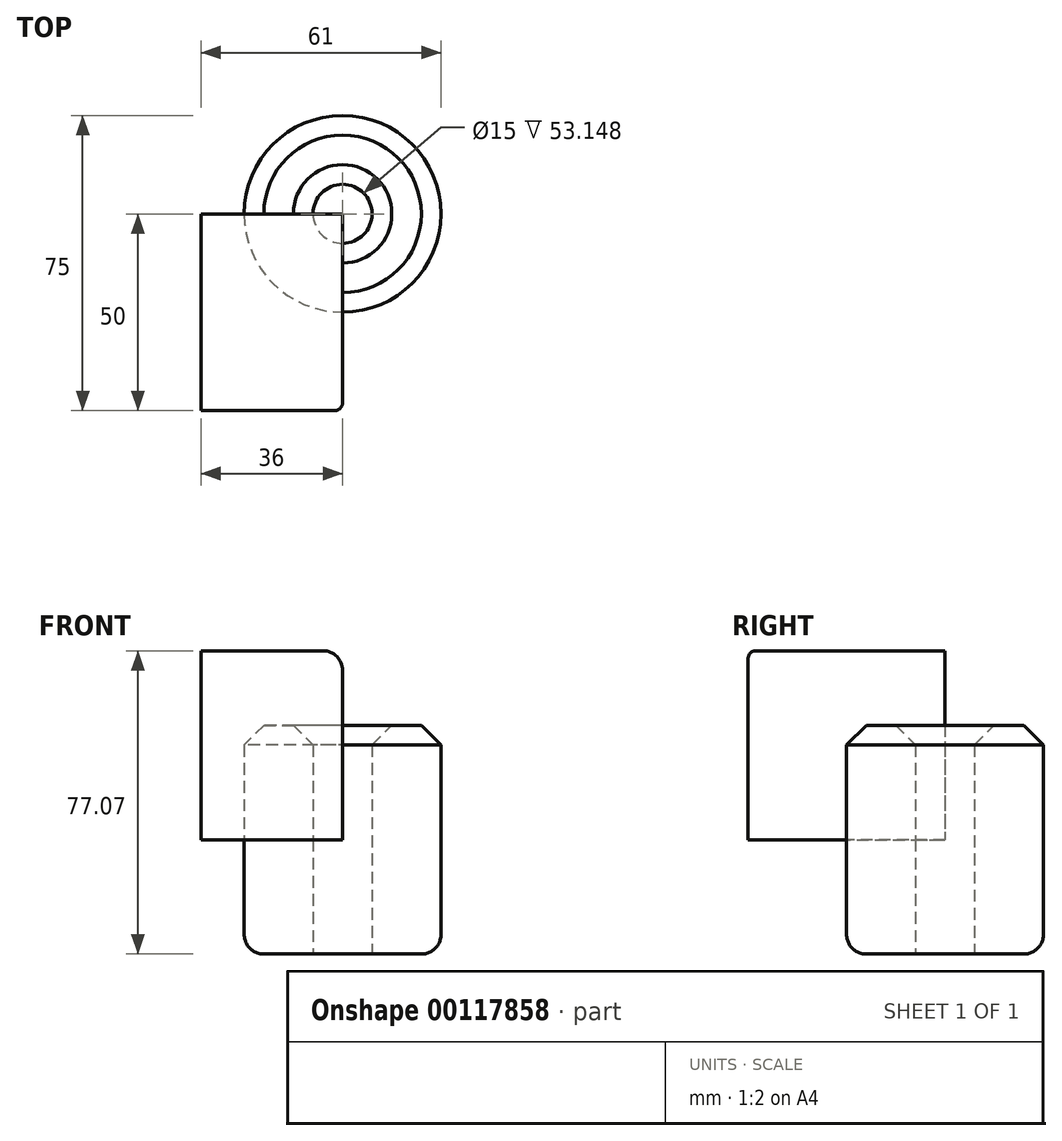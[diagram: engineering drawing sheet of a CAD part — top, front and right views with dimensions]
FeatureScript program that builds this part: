
annotation { "Feature Type Name" : "Feature", "Feature Type Description" : "" }
export const myFeature = defineFeature(function(context is Context, id is Id, definition is map)
    precondition{}
    {
        {
            var Q0;
            Q0=qCreatedBy(makeId("Top.planeOp"),FACE);
            var sketch = newSketch(context, id + "F0", { "sketchPlane" : qUnion([Q0])});
            skCircle(sketch, "E0", {"center": v(0, 0) * mm, "radius": 7.5 * mm});
            skCircle(sketch, "E1", {"center": v(0, 0) * mm, "radius": 25 * mm});
            skSolve(sketch);
        }
        {
            var Q0;
            Q0=makeQuery(id+"F0.imprint","IMPRINT",FACE,{"disambiguationData":[TD([[makeQuery(id+"F0.imprint","IMPRINT",EDGE,{"derivedFrom":sQuery(id+"F0.wireOp",EDGE,"E0")}),-1.0]])]});
            extrude(context, id + "F1", {"entities" : qUnion([Q0]), "endBound" : BoundingType.SYMMETRIC, "depth" : 58.15 * mm});
        }
        {
            var Q0;
            Q0=qCreatedBy(makeId("Front.planeOp"),FACE);
            var sketch = newSketch(context, id + "F2", { "sketchPlane" : qUnion([Q0])});
            skLineSegment(sketch, "E2.bottom", {"start": v(-36, 48) * mm, "end": v(0, 48) * mm});
            skLineSegment(sketch, "E2.top", {"start": v(-36, 0) * mm, "end": v(0, 0) * mm});
            skLineSegment(sketch, "E2.left", {"start": v(-36, 48) * mm, "end": v(-36, 0) * mm});
            skLineSegment(sketch, "E2.right", {"start": v(0, 48) * mm, "end": v(0, 0) * mm});
            skSolve(sketch);
        }
        {
            var Q0;
            Q0=makeQuery(id+"F2.imprint","IMPRINT",FACE,{"disambiguationData":[TD([[makeQuery(id+"F2.imprint","IMPRINT",EDGE,{"derivedFrom":sQuery(id+"F2.wireOp",EDGE,"E2.bottom")}),-1.0]])]});
            extrude(context, id + "F3", {"entities" : qUnion([Q0]), "operationType" : NewBodyOperationType.ADD, "depth" : 50 * mm});
        }
        {
            var Q0;
            Q0=makeQuery(id+"F1.opExtrude","CAP_EDGE",EDGE,{"disambiguationData":[OSD([sQuery(id+"F0.wireOp",EDGE,"E1")])],"isStart":false});
            var Q1;
            Q1=makeQuery(id+"F1.opExtrude","CAP_EDGE",EDGE,{"disambiguationData":[OSD([sQuery(id+"F0.wireOp",EDGE,"E0")])],"isStart":false});
            chamfer(context, id + "F4", {"entities" : qUnion([Q0, Q1]), "width" : 5 * mm, "tangentPropagation" : true});
        }
        {
            var Q0;
            Q0=makeQuery(id+"F3.opExtrude","SWEPT_EDGE",EDGE,{"disambiguationData":[OSD([sQuery(id+"F2.wireOp",EDGE,"E2.bottom"),sQuery(id+"F2.wireOp",EDGE,"E2.right")])]});
            fillet(context, id + "F5", {"entities" : qUnion([Q0]), "radius" : 5 * mm, "tangentPropagation" : true, "allowEdgeOverflow" : false});
        }
        {
            var Q0;
            Q0=makeQuery(id+"F3.opExtrude","CAP_EDGE",EDGE,{"disambiguationData":[OSD([sQuery(id+"F2.wireOp",EDGE,"E2.bottom")])],"isStart":false});
            fillet(context, id + "F6", {"entities" : qUnion([Q0]), "radius" : 2 * mm, "tangentPropagation" : true, "allowEdgeOverflow" : false});
        }
        {
            var Q0;
            Q0=makeQuery(id+"F1.opExtrude","CAP_EDGE",EDGE,{"disambiguationData":[OSD([sQuery(id+"F0.wireOp",EDGE,"E1")])],"isStart":true});
            fillet(context, id + "F7", {"entities" : qUnion([Q0]), "radius" : 5 * mm, "tangentPropagation" : true, "allowEdgeOverflow" : false});
        }
    });
